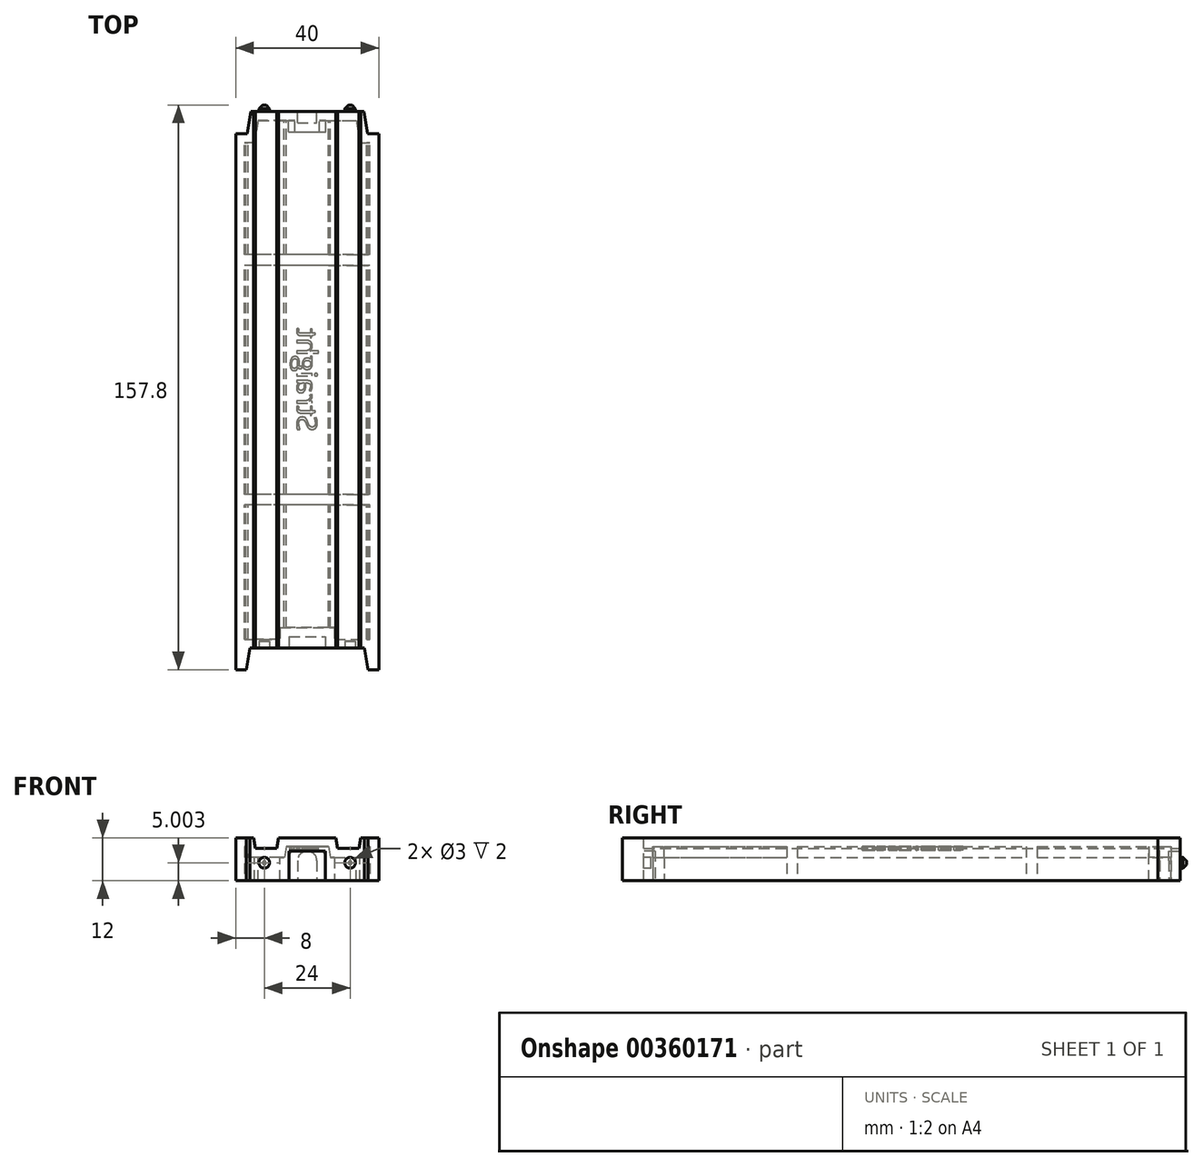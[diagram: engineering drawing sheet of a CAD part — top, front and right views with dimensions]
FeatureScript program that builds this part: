
annotation { "Feature Type Name" : "Feature", "Feature Type Description" : "" }
export const myFeature = defineFeature(function(context is Context, id is Id, definition is map)
    precondition{}
    {
        {
            var Q0;
            Q0=qCreatedBy(makeId("Front.planeOp"),FACE);
            var sketch = newSketch(context, id + "F0", { "sketchPlane" : qUnion([Q0])});
            skLineSegment(sketch, "E0", {"start": v(-20, 6.43) * mm, "end": v(-20, -5.57) * mm});
            skLineSegment(sketch, "E1", {"start": v(-20, -5.57) * mm, "end": v(20, -5.57) * mm});
            skLineSegment(sketch, "E2", {"start": v(20, -5.57) * mm, "end": v(20, 6.43) * mm});
            skLineSegment(sketch, "E3", {"start": v(-8, 6.43) * mm, "end": v(-8.53, 3.43) * mm});
            skLineSegment(sketch, "E4", {"start": v(-8.53, 3.43) * mm, "end": v(-14.47, 3.43) * mm});
            skLineSegment(sketch, "E5", {"start": v(-14.47, 3.43) * mm, "end": v(-15, 6.43) * mm});
            skLineSegment(sketch, "E6", {"start": v(-15, 6.43) * mm, "end": v(-20, 6.43) * mm});
            skLineSegment(sketch, "E7", {"start": v(-11.5, 10.56) * mm, "end": v(-11.5, 0) * mm, "construction": true});
            skLineSegment(sketch, "E8.MirrorCS", {"start": v(8, 6.43) * mm, "end": v(8.53, 3.43) * mm});
            skLineSegment(sketch, "E9.MirrorCS", {"start": v(15, 6.43) * mm, "end": v(20, 6.43) * mm});
            skLineSegment(sketch, "E10.MirrorCS", {"start": v(14.47, 3.43) * mm, "end": v(15, 6.43) * mm});
            skLineSegment(sketch, "E11.MirrorCS", {"start": v(11.5, 10.56) * mm, "end": v(11.5, 0) * mm, "construction": true});
            skLineSegment(sketch, "E12.MirrorCS", {"start": v(8.53, 3.43) * mm, "end": v(14.47, 3.43) * mm});
            skLineSegment(sketch, "E13", {"start": v(-8, 6.43) * mm, "end": v(8, 6.43) * mm});
            skSolve(sketch);
        }
        {
            var Q0;
            Q0 = qSketchRegion(id + "F0", true);
            extrude(context, id + "F1", {"entities" : qUnion([Q0]), "depth" : 150 * mm, "hasSecondDirection" : true, "secondDirectionOppositeDirection" : true, "secondDirectionDepth" : 25 * mm, "symmetric" : true});
        }
        {
            var Q0;
            {var subQ4=sQuery(id+"F0.wireOp",EDGE,"E3");var subQ5=sQuery(id+"F0.wireOp",EDGE,"E13");var subQ6=sQuery(id+"F0.wireOp",EDGE,"E12.MirrorCS");var subQ7=sQuery(id+"F0.wireOp",EDGE,"E1");var subQ8=sQuery(id+"F0.wireOp",EDGE,"E4");var subQ9=sQuery(id+"F0.wireOp",EDGE,"E8.MirrorCS");Q0=makeQuery(id+"FZOg18RNejO7ONX_1.boolean.opBoolean","SPLIT",FACE,{"disambiguationData":[TD([makeQuery(id+"F1.opExtrude","SWEPT_FACE",FACE,{"disambiguationData":[OSD([subQ4])]})])],"derivedFrom":makeQuery(id+"F1.opExtrude","CAP_FACE",FACE,{"disambiguationData":[OSD([sQuery(id+"F0.wireOp",EDGE,"E0"),subQ7,sQuery(id+"F0.wireOp",EDGE,"E2"),subQ4,subQ8,sQuery(id+"F0.wireOp",EDGE,"E5"),sQuery(id+"F0.wireOp",EDGE,"E6"),subQ9,sQuery(id+"F0.wireOp",EDGE,"E9.MirrorCS"),sQuery(id+"F0.wireOp",EDGE,"E10.MirrorCS"),subQ6,subQ5])],"isStart":false})});}
            var sketch = newSketch(context, id + "F2", { "sketchPlane" : qUnion([Q0])});
            skLineSegment(sketch, "E14", {"start": v(-5.1, 0.03) * mm, "end": v(-5.1, -5.57) * mm});
            skLineSegment(sketch, "E15", {"start": v(5.1, 0.03) * mm, "end": v(5.1, -5.57) * mm});
            skLineSegment(sketch, "E16", {"start": v(5.1, -5.57) * mm, "end": v(-5.1, -5.57) * mm});
            skLineSegment(sketch, "E17", {"start": v(-2.4, 2.73) * mm, "end": v(2.4, 2.73) * mm});
            skLineSegment(sketch, "E18", {"start": v(2.4, 2.73) * mm, "end": v(5.1, 2.73) * mm});
            skLineSegment(sketch, "E19", {"start": v(5.1, 2.73) * mm, "end": v(5.1, 0.03) * mm});
            skLineSegment(sketch, "E20", {"start": v(-5.1, 0.03) * mm, "end": v(-5.1, 2.73) * mm});
            skLineSegment(sketch, "E21", {"start": v(-5.1, 2.73) * mm, "end": v(-2.4, 2.73) * mm});
            skSolve(sketch);
        }
        {
            var Q0;
            Q0 = qSketchRegion(id + "F2", true);
            extrude(context, id + "F3", {"entities" : qUnion([Q0]), "operationType" : NewBodyOperationType.REMOVE, "oppositeDirection" : true, "depth" : 3.2 * mm});
        }
        {
            var Q0;
            {var subQ1=sQuery(id+"F0.wireOp",EDGE,"E1");var subQ3=sQuery(id+"F0.wireOp",EDGE,"E3");var subQ4=sQuery(id+"F0.wireOp",EDGE,"E13");var subQ5=sQuery(id+"F0.wireOp",EDGE,"E12.MirrorCS");var subQ6=sQuery(id+"F0.wireOp",EDGE,"E4");var subQ7=sQuery(id+"F0.wireOp",EDGE,"E8.MirrorCS");Q0=makeQuery(id+"Fqij16aE58OMZVd_1.boolean.opBoolean","SPLIT",FACE,{"disambiguationData":[TD([makeQuery(id+"F1.opExtrude","SWEPT_FACE",FACE,{"disambiguationData":[OSD([subQ3])]})])],"derivedFrom":makeQuery(id+"F1.opExtrude","CAP_FACE",FACE,{"disambiguationData":[OSD([sQuery(id+"F0.wireOp",EDGE,"E0"),subQ1,sQuery(id+"F0.wireOp",EDGE,"E2"),subQ3,subQ6,sQuery(id+"F0.wireOp",EDGE,"E5"),sQuery(id+"F0.wireOp",EDGE,"E6"),subQ7,sQuery(id+"F0.wireOp",EDGE,"E9.MirrorCS"),sQuery(id+"F0.wireOp",EDGE,"E10.MirrorCS"),subQ5,subQ4])],"isStart":true})});}
            var sketch = newSketch(context, id + "F4", { "sketchPlane" : qUnion([Q0])});
            skArc(sketch, "E22", {"start": v(2.7, 0) * mm, "mid": v(0, 2.7) * mm, "end": v(-2.7, 0) * mm});
            skLineSegment(sketch, "E23", {"start": v(-2.7, 0) * mm, "end": v(-2.7, -5.57) * mm});
            skPoint(sketch, "E23.endSnap0", {"position": v(0, -5.57) * mm});
            skLineSegment(sketch, "E24", {"start": v(2.7, 0) * mm, "end": v(2.7, -5.57) * mm});
            skLineSegment(sketch, "E25", {"start": v(2.7, -5.57) * mm, "end": v(-2.7, -5.57) * mm});
            skSolve(sketch);
        }
        {
            var Q0;
            Q0 = qSketchRegion(id + "F4", true);
            extrude(context, id + "F5", {"entities" : qUnion([Q0]), "operationType" : NewBodyOperationType.REMOVE, "oppositeDirection" : true, "depth" : 3.2 * mm});
        }
        {
            var Q0;
            Q0=makeQuery(id+"F1.opExtrude","SWEPT_FACE",FACE,{"disambiguationData":[OSD([sQuery(id+"F0.wireOp",EDGE,"E6")])]});
            var sketch = newSketch(context, id + "F6", { "sketchPlane" : qUnion([Q0])});
            skLineSegment(sketch, "E26.bottom", {"start": v(-20, -75) * mm, "end": v(-16, -75) * mm});
            skLineSegment(sketch, "E26.top", {"start": v(-20, -81) * mm, "end": v(-17, -81) * mm});
            skLineSegment(sketch, "E26.left", {"start": v(-20, -75) * mm, "end": v(-20, -81) * mm});
            skLineSegment(sketch, "E26.right", {"start": v(-16, -75) * mm, "end": v(-17, -81) * mm});
            skLineSegment(sketch, "E27.MirrorCS", {"start": v(16, -75) * mm, "end": v(17, -81) * mm});
            skLineSegment(sketch, "E28.MirrorCS", {"start": v(20, -75) * mm, "end": v(20, -81) * mm});
            skLineSegment(sketch, "E29.MirrorCS", {"start": v(20, -81) * mm, "end": v(17, -81) * mm});
            skLineSegment(sketch, "E30.MirrorCS", {"start": v(20, -75) * mm, "end": v(16, -75) * mm});
            skSolve(sketch);
        }
        {
            var Q0;
            Q0 = qSketchRegion(id + "F6", true);
            var Q1;
            Q1=makeQuery(id+"F1.opExtrude","SWEPT_FACE",FACE,{"disambiguationData":[OSD([sQuery(id+"F0.wireOp",EDGE,"E1")])]});
            extrude(context, id + "F7", {"entities" : qUnion([Q0]), "operationType" : NewBodyOperationType.ADD, "endBound" : BoundingType.UP_TO_SURFACE, "oppositeDirection" : true, "endBoundEntityFace" : qUnion([Q1]), "depth" : 25 * mm});
        }
        {
            var Q0;
            Q0=makeQuery(id+"F7.boolean.opBoolean","MERGE",FACE,{"derivedFrom":[makeQuery(id+"F1.opExtrude","SWEPT_FACE",FACE,{"disambiguationData":[OSD([sQuery(id+"F0.wireOp",EDGE,"E6")])]}),makeQuery(id+"F7.opExtrude","CAP_FACE",FACE,{"disambiguationData":[OSD([sQuery(id+"F6.wireOp",EDGE,"E26.bottom"),sQuery(id+"F6.wireOp",EDGE,"E26.top"),sQuery(id+"F6.wireOp",EDGE,"E26.left"),sQuery(id+"F6.wireOp",EDGE,"E26.right")])],"isStart":true})]});
            var sketch = newSketch(context, id + "F8", { "sketchPlane" : qUnion([Q0])});
            skLineSegment(sketch, "E31", {"start": v(-20, 75) * mm, "end": v(-20, 68.8) * mm});
            skLineSegment(sketch, "E32", {"start": v(-20, 68.8) * mm, "end": v(-16.83, 68.8) * mm});
            skLineSegment(sketch, "E33", {"start": v(-16.83, 68.8) * mm, "end": v(-15.8, 75) * mm});
            skLineSegment(sketch, "E34", {"start": v(-15.8, 75) * mm, "end": v(-20, 75) * mm});
            skLineSegment(sketch, "E35.MirrorCS", {"start": v(20, 75) * mm, "end": v(20, 68.8) * mm});
            skLineSegment(sketch, "E36.MirrorCS", {"start": v(20, 68.8) * mm, "end": v(16.83, 68.8) * mm});
            skLineSegment(sketch, "E37.MirrorCS", {"start": v(15.8, 75) * mm, "end": v(20, 75) * mm});
            skLineSegment(sketch, "E38.MirrorCS", {"start": v(16.83, 68.8) * mm, "end": v(15.8, 75) * mm});
            skSolve(sketch);
        }
        {
            var Q0;
            Q0 = qSketchRegion(id + "F8", true);
            extrude(context, id + "F9", {"entities" : qUnion([Q0]), "operationType" : NewBodyOperationType.REMOVE, "endBound" : BoundingType.UP_TO_NEXT, "oppositeDirection" : true, "depth" : 25 * mm});
        }
        {
            var Q0;
            {var subQ0=sQuery(id+"F0.wireOp",EDGE,"E1");Q0=makeQuery(id+"F7.boolean.opBoolean","MERGE",FACE,{"derivedFrom":[makeQuery(id+"F1.opExtrude","SWEPT_FACE",FACE,{"disambiguationData":[OSD([subQ0])]}),makeQuery(id+"F7.opExtrude","CAP_FACE",FACE,{"disambiguationData":[OSD([subQ0]),ownerDisambiguation([makeQuery(id+"F6.imprint","IMPRINT",EDGE,{"derivedFrom":sQuery(id+"F6.wireOp",EDGE,"E26.bottom")})])],"isStart":false}),makeQuery(id+"F7.opExtrude","CAP_FACE",FACE,{"disambiguationData":[OSD([subQ0]),ownerDisambiguation([makeQuery(id+"F6.imprint","IMPRINT",EDGE,{"derivedFrom":sQuery(id+"F6.wireOp",EDGE,"E27.MirrorCS")})])],"isStart":false})]});}
            shell(context, id + "F10", {"entities" : qUnion([Q0]), "thickness" : 2.5 * mm});
        }
        {
            var Q0;
            {var subQ0=sQuery(id+"F0.wireOp",EDGE,"E1");Q0=makeQuery(id+"F7.boolean.opBoolean","MERGE",FACE,{"derivedFrom":[makeQuery(id+"F1.opExtrude","SWEPT_FACE",FACE,{"disambiguationData":[OSD([subQ0])]}),makeQuery(id+"F7.opExtrude","CAP_FACE",FACE,{"disambiguationData":[OSD([subQ0]),ownerDisambiguation([makeQuery(id+"F6.imprint","IMPRINT",EDGE,{"derivedFrom":sQuery(id+"F6.wireOp",EDGE,"E26.bottom")})])],"isStart":false}),makeQuery(id+"F7.opExtrude","CAP_FACE",FACE,{"disambiguationData":[OSD([subQ0]),ownerDisambiguation([makeQuery(id+"F6.imprint","IMPRINT",EDGE,{"derivedFrom":sQuery(id+"F6.wireOp",EDGE,"E27.MirrorCS")})])],"isStart":false})]});}
            var sketch = newSketch(context, id + "F11", { "sketchPlane" : qUnion([Q0])});
            skLineSegment(sketch, "E39.bottom", {"start": v(17.5, 35) * mm, "end": v(-17.5, 35) * mm});
            skLineSegment(sketch, "E39.top", {"start": v(17.5, 32) * mm, "end": v(-17.5, 32) * mm});
            skLineSegment(sketch, "E39.left", {"start": v(17.5, 35) * mm, "end": v(17.5, 32) * mm});
            skLineSegment(sketch, "E39.right", {"start": v(-17.5, 35) * mm, "end": v(-17.5, 32) * mm});
            skLineSegment(sketch, "E40.MirrorCS", {"start": v(17.5, -35) * mm, "end": v(17.5, -32) * mm});
            skLineSegment(sketch, "E41.MirrorCS", {"start": v(-17.5, -35) * mm, "end": v(-17.5, -32) * mm});
            skLineSegment(sketch, "E42.MirrorCS", {"start": v(17.5, -32) * mm, "end": v(-17.5, -32) * mm});
            skLineSegment(sketch, "E43.MirrorCS", {"start": v(17.5, -35) * mm, "end": v(-17.5, -35) * mm});
            skSolve(sketch);
        }
        {
            var Q0;
            Q0 = qSketchRegion(id + "F11", true);
            var Q1;
            Q1=makeQuery(id+"F10.opShell","OFFSET_FACE",FACE,{"disambiguationData":[OSD([sQuery(id+"F0.wireOp",EDGE,"E13")])]});
            extrude(context, id + "F12", {"entities" : qUnion([Q0]), "operationType" : NewBodyOperationType.ADD, "endBound" : BoundingType.UP_TO_SURFACE, "oppositeDirection" : true, "endBoundEntityFace" : qUnion([Q1]), "depth" : 25 * mm});
        }
        {
            var Q0;
            Q0=makeQuery(id+"F1.opExtrude","CAP_FACE",FACE,{"disambiguationData":[OSD([sQuery(id+"F0.wireOp",EDGE,"E0"),sQuery(id+"F0.wireOp",EDGE,"E1"),sQuery(id+"F0.wireOp",EDGE,"E2"),sQuery(id+"F0.wireOp",EDGE,"E3"),sQuery(id+"F0.wireOp",EDGE,"E4"),sQuery(id+"F0.wireOp",EDGE,"E5"),sQuery(id+"F0.wireOp",EDGE,"E6"),sQuery(id+"F0.wireOp",EDGE,"E8.MirrorCS"),sQuery(id+"F0.wireOp",EDGE,"E9.MirrorCS"),sQuery(id+"F0.wireOp",EDGE,"E10.MirrorCS"),sQuery(id+"F0.wireOp",EDGE,"E12.MirrorCS"),sQuery(id+"F0.wireOp",EDGE,"E13")])],"isStart":false});
            var sketch = newSketch(context, id + "F13", { "sketchPlane" : qUnion([Q0])});
            skLineSegment(sketch, "E44.0", {"start": v(-14.47, 3.43) * mm, "end": v(-15, 6.43) * mm});
            skLineSegment(sketch, "E44.1", {"start": v(-8.53, 3.43) * mm, "end": v(-14.47, 3.43) * mm});
            skLineSegment(sketch, "E44.2", {"start": v(-8, 6.43) * mm, "end": v(-8.53, 3.43) * mm});
            skLineSegment(sketch, "E44.3", {"start": v(8, 6.43) * mm, "end": v(8.53, 3.43) * mm});
            skLineSegment(sketch, "E44.4", {"start": v(8.53, 3.43) * mm, "end": v(14.47, 3.43) * mm});
            skLineSegment(sketch, "E44.5", {"start": v(14.47, 3.43) * mm, "end": v(15, 6.43) * mm});
            skPoint(sketch, "E44.6", {"position": v(-14.74, 4.93) * mm});
            skLineSegment(sketch, "E45", {"start": v(8, 6.43) * mm, "end": v(15, 6.43) * mm});
            skLineSegment(sketch, "E46", {"start": v(-15, 6.43) * mm, "end": v(-8, 6.43) * mm});
            skSolve(sketch);
        }
        {
            var Q0;
            Q0 = qSketchRegion(id + "F13", true);
            var Q1;
            Q1=makeQuery(id+"F1.opExtrude","CAP_FACE",FACE,{"disambiguationData":[OSD([sQuery(id+"F0.wireOp",EDGE,"E0"),sQuery(id+"F0.wireOp",EDGE,"E1"),sQuery(id+"F0.wireOp",EDGE,"E2"),sQuery(id+"F0.wireOp",EDGE,"E3"),sQuery(id+"F0.wireOp",EDGE,"E4"),sQuery(id+"F0.wireOp",EDGE,"E5"),sQuery(id+"F0.wireOp",EDGE,"E6"),sQuery(id+"F0.wireOp",EDGE,"E8.MirrorCS"),sQuery(id+"F0.wireOp",EDGE,"E9.MirrorCS"),sQuery(id+"F0.wireOp",EDGE,"E10.MirrorCS"),sQuery(id+"F0.wireOp",EDGE,"E12.MirrorCS"),sQuery(id+"F0.wireOp",EDGE,"E13")])],"isStart":true});
            extrude(context, id + "F14", {"entities" : qUnion([Q0]), "operationType" : NewBodyOperationType.REMOVE, "endBound" : BoundingType.UP_TO_SURFACE, "oppositeDirection" : true, "endBoundEntityFace" : qUnion([Q1]), "depth" : 25 * mm});
        }
        {
            var Q0;
            Q0=makeQuery(id+"F12.boolean.opBoolean","SPLIT",FACE,{"disambiguationData":[TD([makeQuery(id+"F12.opExtrude","SWEPT_FACE",FACE,{"disambiguationData":[OSD([sQuery(id+"F11.wireOp",EDGE,"E39.top")])]})])],"derivedFrom":makeQuery(id+"F10.opShell","OFFSET_FACE",FACE,{"disambiguationData":[OSD([sQuery(id+"F0.wireOp",EDGE,"E13")])]})});
            var sketch = newSketch(context, id + "F15", { "sketchPlane" : qUnion([Q0])});
            skText(sketch, "E47", { "text": "Straight", "fontName": "OpenSans-Regular.ttf"});
            const initialGuessF15  = {"E47": [-0.0029, 0.01434, 0, -1, 0.0057]};
            skSetInitialGuess(sketch, initialGuessF15);
            skSolve(sketch);
        }
        {
            var Q0;
            Q0 = qSketchRegion(id + "F15", true);
            extrude(context, id + "F16", {"entities" : qUnion([Q0]), "operationType" : NewBodyOperationType.ADD, "depth" : 1 * mm});
        }
        {
            var Q0;
            Q0=makeQuery(id+"F1.opExtrude","CAP_FACE",FACE,{"disambiguationData":[OSD([sQuery(id+"F0.wireOp",EDGE,"E0"),sQuery(id+"F0.wireOp",EDGE,"E1"),sQuery(id+"F0.wireOp",EDGE,"E2"),sQuery(id+"F0.wireOp",EDGE,"E3"),sQuery(id+"F0.wireOp",EDGE,"E4"),sQuery(id+"F0.wireOp",EDGE,"E5"),sQuery(id+"F0.wireOp",EDGE,"E6"),sQuery(id+"F0.wireOp",EDGE,"E8.MirrorCS"),sQuery(id+"F0.wireOp",EDGE,"E9.MirrorCS"),sQuery(id+"F0.wireOp",EDGE,"E10.MirrorCS"),sQuery(id+"F0.wireOp",EDGE,"E12.MirrorCS"),sQuery(id+"F0.wireOp",EDGE,"E13")])],"isStart":false});
            var sketch = newSketch(context, id + "F17", { "sketchPlane" : qUnion([Q0])});
            skCircle(sketch, "E48", {"center": v(-12, -0.57) * mm, "radius": 1.5 * mm});
            skCircle(sketch, "E49.MirrorC", {"center": v(12, -0.57) * mm, "radius": 1.5 * mm});
            skSolve(sketch);
        }
        {
            var Q0;
            Q0 = qSketchRegion(id + "F17", true);
            extrude(context, id + "F18", {"entities" : qUnion([Q0]), "operationType" : NewBodyOperationType.REMOVE, "oppositeDirection" : true, "depth" : 2 * mm});
        }
        {
            var Q0;
            Q0=makeQuery(id+"F1.opExtrude","CAP_FACE",FACE,{"disambiguationData":[OSD([sQuery(id+"F0.wireOp",EDGE,"E0"),sQuery(id+"F0.wireOp",EDGE,"E1"),sQuery(id+"F0.wireOp",EDGE,"E2"),sQuery(id+"F0.wireOp",EDGE,"E3"),sQuery(id+"F0.wireOp",EDGE,"E4"),sQuery(id+"F0.wireOp",EDGE,"E5"),sQuery(id+"F0.wireOp",EDGE,"E6"),sQuery(id+"F0.wireOp",EDGE,"E8.MirrorCS"),sQuery(id+"F0.wireOp",EDGE,"E9.MirrorCS"),sQuery(id+"F0.wireOp",EDGE,"E10.MirrorCS"),sQuery(id+"F0.wireOp",EDGE,"E12.MirrorCS"),sQuery(id+"F0.wireOp",EDGE,"E13")])],"isStart":true});
            var sketch = newSketch(context, id + "F19", { "sketchPlane" : qUnion([Q0])});
            skCircle(sketch, "E50", {"center": v(-12, -0.57) * mm, "radius": 1.5 * mm});
            skCircle(sketch, "E51.MirrorC", {"center": v(12, -0.57) * mm, "radius": 1.5 * mm});
            skSolve(sketch);
        }
        {
            var Q0;
            Q0 = qSketchRegion(id + "F19", true);
            extrude(context, id + "F20", {"entities" : qUnion([Q0]), "operationType" : NewBodyOperationType.ADD, "depth" : 1.8 * mm});
        }
        {
            var Q0;
            Q0=makeQuery(id+"F20.opExtrude","CAP_EDGE",EDGE,{"disambiguationData":[OSD([sQuery(id+"F19.wireOp",EDGE,"E50")])],"isStart":false});
            var Q1;
            Q1=makeQuery(id+"F20.opExtrude","CAP_EDGE",EDGE,{"disambiguationData":[OSD([sQuery(id+"F19.wireOp",EDGE,"E51.MirrorC")])],"isStart":false});
            chamfer(context, id + "F21", {"entities" : qUnion([Q0, Q1]), "width" : 1 * mm, "tangentPropagation" : true});
        }
    });
